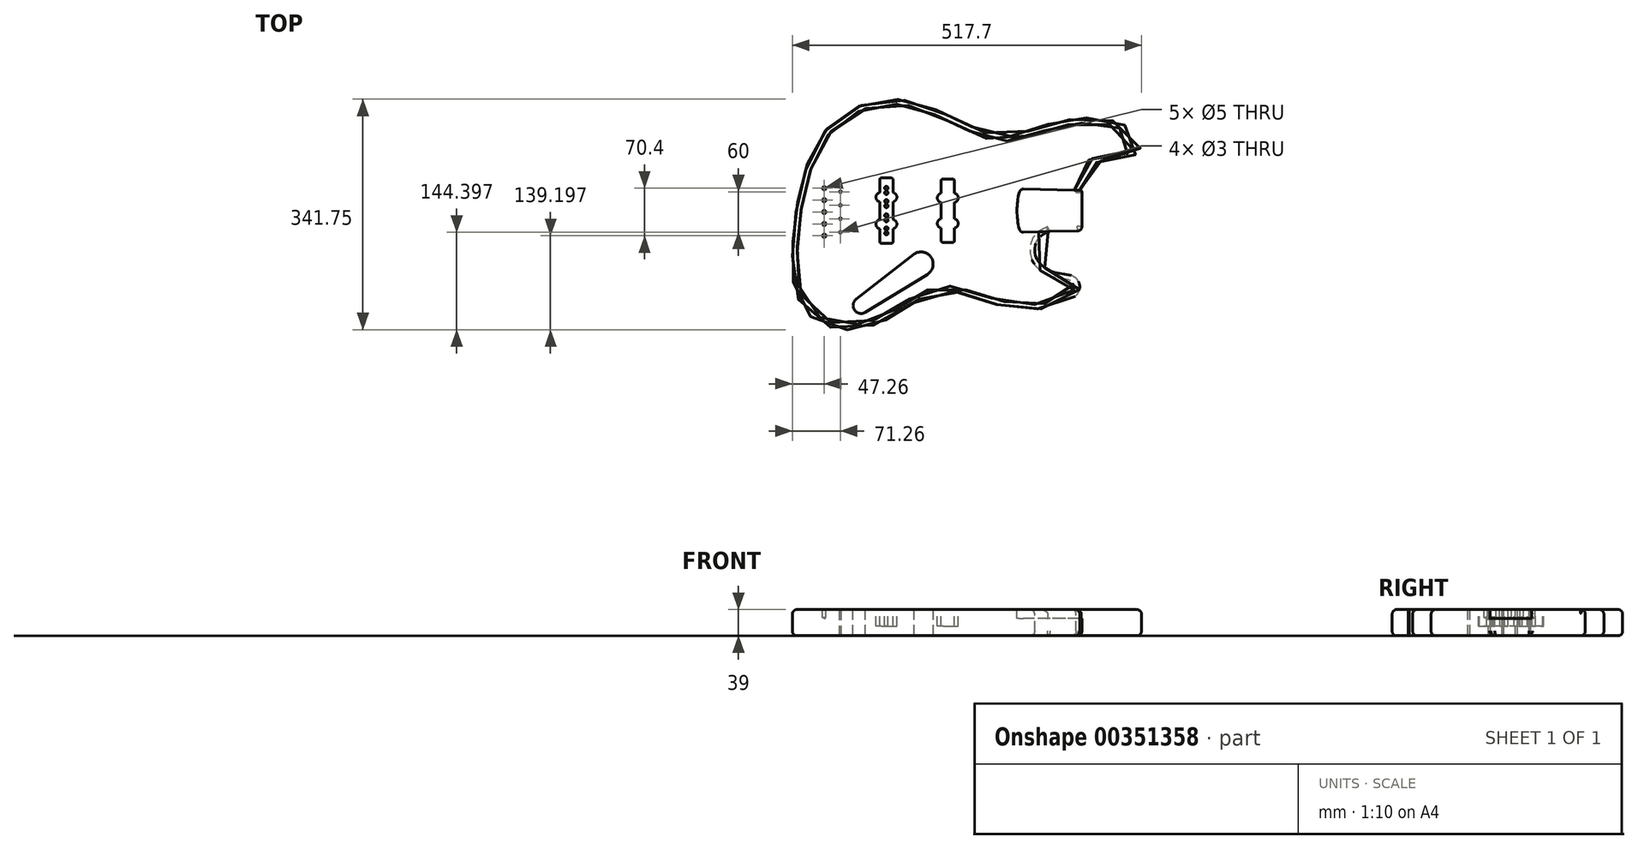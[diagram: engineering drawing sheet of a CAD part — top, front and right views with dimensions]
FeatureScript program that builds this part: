
annotation { "Feature Type Name" : "Feature", "Feature Type Description" : "" }
export const myFeature = defineFeature(function(context is Context, id is Id, definition is map)
    precondition{}
    {
        {
            var Q0;
            Q0=qCreatedBy(makeId("Top.planeOp"),FACE);
            var sketch = newSketch(context, id + "F0", { "sketchPlane" : qUnion([Q0])});
            skSolve(sketch);
        }
        {
            var Q0;
            Q0=qCreatedBy(makeId("Top.planeOp"),FACE);
            var sketch = newSketch(context, id + "F1", { "sketchPlane" : qUnion([Q0])});
            skFitSpline(sketch, "E0", {"points": [v(289.6, -29.05) * mm, v(282.8, -32.55) * mm, v(274.5, -39.46) * mm, v(271.1, -45.26) * mm, v(269.09, -54.77) * mm, v(271.6, -68.78) * mm, v(280.6, -80.18) * mm, v(290.16, -86.66) * mm, v(298.23, -89.68) * mm, v(304.15, -90.57) * mm, v(313.74, -92.33) * mm, v(322.81, -94.1) * mm, v(331, -99.01) * mm, v(334.35, -104.33) * mm, v(335.78, -110.76) * mm, v(333.88, -119.56) * mm, v(327.1, -126.94) * mm, v(314.12, -135.03) * mm, v(295.68, -140.86) * mm, v(270.69, -144.08) * mm, v(240.34, -142.89) * mm, v(209.4, -136.58) * mm, v(186.79, -130.03) * mm, v(168.58, -123.49) * mm, v(156.92, -119.44) * mm, v(143.35, -116.94) * mm, v(129.19, -117.66) * mm, v(110.88, -123.12) * mm, v(92.1, -132.54) * mm, v(78.73, -141.94) * mm, v(63.02, -151.93) * mm, v(42.08, -162.88) * mm, v(24.35, -170.02) * mm, v(7.93, -173.23) * mm, v(-6.83, -174.54) * mm, v(-29.2, -172.4) * mm, v(-58.12, -159.2) * mm, v(-74.3, -142.3) * mm, v(-85.73, -119.2) * mm, v(-89.54, -95.05) * mm, v(-90.25, -74.22) * mm, v(-89.42, -41.97) * mm, v(-86.33, -8.53) * mm, v(-81.57, 19.8) * mm, v(-72.28, 56.92) * mm, v(-59.79, 92.15) * mm, v(-48.36, 111.66) * mm, v(-27.9, 133.92) * mm, v(-3.38, 151.05) * mm, v(21.25, 161.29) * mm, v(43.5, 166.17) * mm, v(72.9, 166.17) * mm, v(111.46, 155.81) * mm, v(140.02, 143.2) * mm, v(171.8, 127.97) * mm, v(186.79, 121.06) * mm, v(202.97, 114.88) * mm, v(219.75, 112.02) * mm, v(234.99, 112.73) * mm, v(257.36, 119.16) * mm, v(282.59, 127.73) * mm, v(302.82, 133.2) * mm, v(323.88, 137.37) * mm, v(345.06, 139.15) * mm, v(365.65, 138.68) * mm, v(387.9, 134.27) * mm, v(404.69, 127.73) * mm, v(415.16, 121.18) * mm, v(423.73, 112.85) * mm, v(427.3, 104.4) * mm, v(425.87, 95) * mm, v(418.5, 85.24) * mm, v(409.8, 80.25) * mm, v(397.66, 78.1) * mm, v(378.74, 76.44) * mm, v(363.27, 74.18) * mm, v(349.47, 69.77) * mm, v(340.78, 65.6) * mm, v(332.33, 56.09) * mm, v(330.55, 47.4) * mm, v(331.5, 40.02) * mm, v(334.23, 35.26) * mm, v(339, 31.7) * mm], "startDerivative": vector(-807.17, -361.43) * mm, "endDerivative": vector(723.85, -461.92) * mm});
            skLineSegment(sketch, "E1", {"start": v(339, 31.7) * mm, "end": v(339, -27.97) * mm});
            skLineSegment(sketch, "E2", {"start": v(289.6, -29.05) * mm, "end": v(339, -27.97) * mm});
            skSolve(sketch);
        }
        {
            var Q0;
            Q0=makeQuery(id+"F1.imprint","IMPRINT",FACE,{"disambiguationData":[TD([[makeQuery(id+"F1.imprint","IMPRINT",EDGE,{"derivedFrom":sQuery(id+"F1.wireOp",EDGE,"E0")}),-1.0]])]});
            extrude(context, id + "F2", {"entities" : qUnion([Q0]), "oppositeDirection" : true, "depth" : 39 * mm});
        }
        {
            var Q0;
            Q0=makeQuery(id+"F2.opExtrude","CAP_EDGE",EDGE,{"disambiguationData":[OSD([sQuery(id+"F1.wireOp",EDGE,"E0")])],"isStart":true});
            var Q1;
            Q1=makeQuery(id+"F2.opExtrude","CAP_EDGE",EDGE,{"disambiguationData":[OSD([sQuery(id+"F1.wireOp",EDGE,"E0")])],"isStart":false});
            var Q2;
            Q2=makeQuery(id+"F2.opExtrude","CAP_EDGE",EDGE,{"disambiguationData":[OSD([sQuery(id+"F1.wireOp",EDGE,"E2")])],"isStart":false});
            var Q3;
            Q3=makeQuery(id+"F2.opExtrude","CAP_EDGE",EDGE,{"disambiguationData":[OSD([sQuery(id+"F1.wireOp",EDGE,"E1")])],"isStart":false});
            fillet(context, id + "F3", {"entities" : qUnion([Q0, Q1, Q2, Q3]), "radius" : 7 * mm, "tangentPropagation" : true, "allowEdgeOverflow" : false});
        }
        {
            var Q0;
            Q0=qCreatedBy(makeId("Top.planeOp"),FACE);
            var sketch = newSketch(context, id + "F4", { "sketchPlane" : qUnion([Q0])});
            skLineSegment(sketch, "E3", {"start": v(346.15, -28.2) * mm, "end": v(247.58, -30.26) * mm});
            skLineSegment(sketch, "E4", {"start": v(247.58, 1.8) * mm, "end": v(247.58, -30.26) * mm, "construction": true});
            skArc(sketch, "E5", {"start": v(242.72, 1.8) * mm, "mid": v(243.94, -14.41) * mm, "end": v(247.58, -30.26) * mm});
            skLineSegment(sketch, "E6", {"start": v(346.15, 1.8) * mm, "end": v(346.15, -28.2) * mm});
            skLineSegment(sketch, "E7", {"start": v(368.55, 1.8) * mm, "end": v(71.57, 1.8) * mm, "construction": true});
            skLineSegment(sketch, "E8.MirrorCS", {"start": v(346.15, 31.8) * mm, "end": v(247.58, 33.85) * mm});
            skArc(sketch, "E9.MirrorCS", {"start": v(242.72, 1.8) * mm, "mid": v(243.94, 18) * mm, "end": v(247.58, 33.85) * mm});
            skLineSegment(sketch, "E10.MirrorCS", {"start": v(346.15, 1.8) * mm, "end": v(346.15, 31.8) * mm});
            skLineSegment(sketch, "E11", {"start": v(71.57, 1.8) * mm, "end": v(-104.88, 1.8) * mm, "construction": true});
            skSolve(sketch);
        }
        {
            var Q0;
            Q0 = qSketchRegion(id + "F4", true);
            extrude(context, id + "F5", {"entities" : qUnion([Q0]), "operationType" : NewBodyOperationType.REMOVE, "oppositeDirection" : true, "depth" : 13 * mm});
        }
        {
            var Q0;
            Q0=makeQuery(id+"F2.opExtrude","SWEPT_EDGE",EDGE,{"disambiguationData":[OSD([sQuery(id+"F1.wireOp",EDGE,"E0"),sQuery(id+"F1.wireOp",EDGE,"E2")])]});
            fillet(context, id + "F6", {"entities" : qUnion([Q0]), "radius" : 10 * mm, "tangentPropagation" : true, "allowEdgeOverflow" : false});
        }
        {
            var Q0;
            Q0=makeQuery(id+"F2.opExtrude","SWEPT_EDGE",EDGE,{"disambiguationData":[OSD([sQuery(id+"F1.wireOp",EDGE,"E1"),sQuery(id+"F1.wireOp",EDGE,"E2")])]});
            var Q1;
            Q1=makeQuery(id+"F2.opExtrude","SWEPT_EDGE",EDGE,{"disambiguationData":[OSD([sQuery(id+"F1.wireOp",EDGE,"E0"),sQuery(id+"F1.wireOp",EDGE,"E1")])]});
            fillet(context, id + "F7", {"entities" : qUnion([Q0, Q1]), "radius" : 6 * mm, "tangentPropagation" : true, "allowEdgeOverflow" : false});
        }
        {
            var Q0;
            Q0=makeQuery(id+"F5.boolean.opBoolean","COPY",EDGE,{"derivedFrom":makeQuery(id+"F5.opExtrude","SWEPT_EDGE",EDGE,{"disambiguationData":[OSD([sQuery(id+"F4.wireOp",EDGE,"E8.MirrorCS"),sQuery(id+"F4.wireOp",EDGE,"E9.MirrorCS")])]})});
            var Q1;
            Q1=makeQuery(id+"F5.boolean.opBoolean","COPY",EDGE,{"derivedFrom":makeQuery(id+"F5.opExtrude","SWEPT_EDGE",EDGE,{"disambiguationData":[OSD([sQuery(id+"F4.wireOp",EDGE,"E3"),sQuery(id+"F4.wireOp",EDGE,"E5")])]})});
            fillet(context, id + "F8", {"entities" : qUnion([Q0, Q1]), "radius" : 6 * mm, "tangentPropagation" : true, "allowEdgeOverflow" : false});
        }
        {
            var Q0;
            Q0=qCreatedBy(makeId("Top.planeOp"),FACE);
            var sketch = newSketch(context, id + "F9", { "sketchPlane" : qUnion([Q0])});
            skLineSegment(sketch, "E12.bottom", {"start": v(40.12, 49.3) * mm, "end": v(58.12, 49.3) * mm, "construction": true});
            skLineSegment(sketch, "E12.left", {"start": v(40.12, 49.3) * mm, "end": v(40.12, 27.8) * mm, "construction": true});
            skLineSegment(sketch, "E12.right", {"start": v(58.12, 49.3) * mm, "end": v(58.12, 27.8) * mm, "construction": true});
            skLineSegment(sketch, "E13", {"start": v(40.12, 21.8) * mm, "end": v(58.12, 21.8) * mm, "construction": true});
            skArc(sketch, "E14", {"start": v(58.12, 15.8) * mm, "mid": v(63.62, 21.8) * mm, "end": v(58.12, 27.8) * mm, "construction": true});
            skLineSegment(sketch, "E15", {"start": v(49.12, 49.3) * mm, "end": v(49.12, 1.8) * mm, "construction": true});
            skLineSegment(sketch, "E16.trimOffspring", {"start": v(58.12, 15.8) * mm, "end": v(58.12, 1.8) * mm, "construction": true});
            skArc(sketch, "E17.MirrorCS", {"start": v(40.12, 15.8) * mm, "mid": v(34.62, 21.8) * mm, "end": v(40.12, 27.8) * mm, "construction": true});
            skLineSegment(sketch, "E18.trimOffspring", {"start": v(40.12, 15.8) * mm, "end": v(40.12, 1.8) * mm, "construction": true});
            skLineSegment(sketch, "E19.MirrorCS", {"start": v(40.12, -12.2) * mm, "end": v(40.12, 1.8) * mm, "construction": true});
            skArc(sketch, "E20.MirrorCS", {"start": v(40.12, -12.2) * mm, "mid": v(34.62, -18.2) * mm, "end": v(40.12, -24.2) * mm, "construction": true});
            skLineSegment(sketch, "E21.MirrorCS", {"start": v(40.12, -45.7) * mm, "end": v(40.12, -24.2) * mm, "construction": true});
            skLineSegment(sketch, "E22.MirrorCS", {"start": v(40.12, -45.7) * mm, "end": v(58.12, -45.7) * mm, "construction": true});
            skLineSegment(sketch, "E23.MirrorCS", {"start": v(58.12, -45.7) * mm, "end": v(58.12, -24.2) * mm, "construction": true});
            skArc(sketch, "E24.MirrorCS", {"start": v(58.12, -12.2) * mm, "mid": v(63.62, -18.2) * mm, "end": v(58.12, -24.2) * mm, "construction": true});
            skLineSegment(sketch, "E25.MirrorCS", {"start": v(58.12, -12.2) * mm, "end": v(58.12, 1.8) * mm, "construction": true});
            skLineSegment(sketch, "E26.0", {"start": v(39.12, 50.3) * mm, "end": v(39.12, 28.65) * mm});
            skArc(sketch, "E26.1", {"start": v(39.12, 14.94) * mm, "mid": v(33.62, 21.8) * mm, "end": v(39.12, 28.65) * mm});
            skLineSegment(sketch, "E26.2", {"start": v(39.12, 14.94) * mm, "end": v(39.12, 1.8) * mm});
            skLineSegment(sketch, "E26.3", {"start": v(59.12, -11.35) * mm, "end": v(59.12, 1.8) * mm});
            skLineSegment(sketch, "E26.4", {"start": v(59.12, 14.94) * mm, "end": v(59.12, 1.8) * mm});
            skArc(sketch, "E26.5", {"start": v(59.12, 14.94) * mm, "mid": v(64.62, 21.8) * mm, "end": v(59.12, 28.65) * mm});
            skLineSegment(sketch, "E26.6", {"start": v(59.12, 50.3) * mm, "end": v(59.12, 28.65) * mm});
            skArc(sketch, "E26.7", {"start": v(59.12, -11.35) * mm, "mid": v(64.62, -18.2) * mm, "end": v(59.12, -25.06) * mm});
            skLineSegment(sketch, "E26.8", {"start": v(59.12, -46.7) * mm, "end": v(59.12, -25.06) * mm});
            skLineSegment(sketch, "E26.9", {"start": v(39.12, -46.7) * mm, "end": v(59.12, -46.7) * mm});
            skLineSegment(sketch, "E26.10", {"start": v(39.12, 50.3) * mm, "end": v(59.12, 50.3) * mm});
            skLineSegment(sketch, "E26.11", {"start": v(39.12, -46.7) * mm, "end": v(39.12, -25.06) * mm});
            skArc(sketch, "E26.12", {"start": v(39.12, -11.35) * mm, "mid": v(33.62, -18.2) * mm, "end": v(39.12, -25.06) * mm});
            skLineSegment(sketch, "E26.13", {"start": v(39.12, -11.35) * mm, "end": v(39.12, 1.8) * mm});
            skLineSegment(sketch, "E27.bottom", {"start": v(131.12, 47.8) * mm, "end": v(149.12, 47.8) * mm, "construction": true});
            skLineSegment(sketch, "E27.top", {"start": v(131.12, -44.2) * mm, "end": v(149.12, -44.2) * mm, "construction": true});
            skLineSegment(sketch, "E27.left", {"start": v(131.12, 47.8) * mm, "end": v(131.12, 26.8) * mm, "construction": true});
            skLineSegment(sketch, "E27.right", {"start": v(149.12, 47.8) * mm, "end": v(149.12, 26.8) * mm, "construction": true});
            skPoint(sketch, "E28", {"position": v(149.12, 1.8) * mm});
            skArc(sketch, "E29", {"start": v(149.12, 14.8) * mm, "mid": v(154.62, 20.8) * mm, "end": v(149.12, 26.8) * mm, "construction": true});
            skLineSegment(sketch, "E30", {"start": v(140.12, 47.8) * mm, "end": v(140.12, -44.2) * mm, "construction": true});
            skArc(sketch, "E31.MirrorCS", {"start": v(131.12, 14.8) * mm, "mid": v(125.62, 20.8) * mm, "end": v(131.12, 26.8) * mm, "construction": true});
            skArc(sketch, "E32.MirrorCS", {"start": v(131.12, -11.2) * mm, "mid": v(125.62, -17.2) * mm, "end": v(131.12, -23.2) * mm, "construction": true});
            skArc(sketch, "E33.MirrorCS", {"start": v(149.12, -11.2) * mm, "mid": v(154.62, -17.2) * mm, "end": v(149.12, -23.2) * mm, "construction": true});
            skLineSegment(sketch, "E34.trimOffspring", {"start": v(131.12, 14.8) * mm, "end": v(131.12, -11.2) * mm, "construction": true});
            skLineSegment(sketch, "E35.trimOffspring", {"start": v(149.12, 14.8) * mm, "end": v(149.12, -11.2) * mm, "construction": true});
            skLineSegment(sketch, "E36.trimOffspring", {"start": v(149.12, -23.2) * mm, "end": v(149.12, -44.2) * mm, "construction": true});
            skLineSegment(sketch, "E37.trimOffspring", {"start": v(131.12, -23.2) * mm, "end": v(131.12, -44.2) * mm, "construction": true});
            skLineSegment(sketch, "E38.0", {"start": v(130.12, 48.8) * mm, "end": v(130.12, 27.65) * mm});
            skArc(sketch, "E38.1", {"start": v(150.12, -10.35) * mm, "mid": v(155.62, -17.2) * mm, "end": v(150.12, -24.06) * mm});
            skLineSegment(sketch, "E38.2", {"start": v(150.12, 13.94) * mm, "end": v(150.12, -10.35) * mm});
            skArc(sketch, "E38.3", {"start": v(150.12, 13.94) * mm, "mid": v(155.62, 20.8) * mm, "end": v(150.12, 27.65) * mm});
            skLineSegment(sketch, "E38.4", {"start": v(150.12, 48.8) * mm, "end": v(150.12, 27.65) * mm});
            skLineSegment(sketch, "E38.5", {"start": v(150.12, -24.06) * mm, "end": v(150.12, -45.2) * mm});
            skLineSegment(sketch, "E38.6", {"start": v(130.12, 48.8) * mm, "end": v(150.12, 48.8) * mm});
            skLineSegment(sketch, "E38.7", {"start": v(130.12, -45.2) * mm, "end": v(150.12, -45.2) * mm});
            skLineSegment(sketch, "E38.8", {"start": v(130.12, -24.06) * mm, "end": v(130.12, -45.2) * mm});
            skArc(sketch, "E38.9", {"start": v(130.12, -10.35) * mm, "mid": v(124.62, -17.2) * mm, "end": v(130.12, -24.06) * mm});
            skLineSegment(sketch, "E38.10", {"start": v(130.12, 13.94) * mm, "end": v(130.12, -10.35) * mm});
            skArc(sketch, "E38.11", {"start": v(130.12, 13.94) * mm, "mid": v(124.62, 20.8) * mm, "end": v(130.12, 27.65) * mm});
            skCircle(sketch, "E39", {"center": v(49.12, 35.3) * mm, "radius": 2.5 * mm});
            skCircle(sketch, "E40", {"center": v(49.12, 28.3) * mm, "radius": 2.5 * mm});
            skLineSegment(sketch, "E41", {"start": v(49.12, 35.3) * mm, "end": v(49.12, 28.3) * mm, "construction": true});
            skPoint(sketch, "E42", {"position": v(49.12, 31.8) * mm});
            skCircle(sketch, "E43.0.1.0", {"center": v(49.12, 15.8) * mm, "radius": 2.5 * mm});
            skCircle(sketch, "E43.0.1.1", {"center": v(49.12, 8.8) * mm, "radius": 2.5 * mm});
            skLineSegment(sketch, "E43.direction1", {"start": v(49.12, 35.3) * mm, "end": v(74.12, 35.3) * mm, "construction": true});
            skLineSegment(sketch, "E43.direction2", {"start": v(49.12, 35.3) * mm, "end": v(49.12, 15.8) * mm, "construction": true});
            skCircle(sketch, "E44.MirrorC", {"center": v(49.12, -31.7) * mm, "radius": 2.5 * mm});
            skCircle(sketch, "E45.MirrorC", {"center": v(49.12, -24.7) * mm, "radius": 2.5 * mm});
            skCircle(sketch, "E46.MirrorC", {"center": v(49.12, -12.2) * mm, "radius": 2.5 * mm});
            skCircle(sketch, "E47.MirrorC", {"center": v(49.12, -5.2) * mm, "radius": 2.5 * mm});
            skSolve(sketch);
        }
        {
            var Q0;
            Q0 = qSketchRegion(id + "F9", true);
            extrude(context, id + "F10", {"entities" : qUnion([Q0]), "operationType" : NewBodyOperationType.REMOVE, "oppositeDirection" : true, "depth" : 25 * mm});
        }
        {
            var Q0;
            Q0=qCreatedBy(makeId("Top.planeOp"),FACE);
            var sketch = newSketch(context, id + "F11", { "sketchPlane" : qUnion([Q0])});
            skPoint(sketch, "E48", {"position": v(-43, 35) * mm});
            skPoint(sketch, "E49.0.1.0", {"position": v(-43, 17.4) * mm});
            skPoint(sketch, "E49.0.2.0", {"position": v(-43, -0.2) * mm});
            skPoint(sketch, "E49.0.3.0", {"position": v(-43, -17.8) * mm});
            skPoint(sketch, "E49.0.4.0", {"position": v(-43, -35.4) * mm});
            skLineSegment(sketch, "E49.direction1", {"start": v(-43, 35) * mm, "end": v(-17.85, 35) * mm, "construction": true});
            skLineSegment(sketch, "E49.direction2", {"start": v(-43, 35) * mm, "end": v(-43, 17.4) * mm, "construction": true});
            skSolve(sketch);
        }
        {
            var Q0;
            Q0=sQuery(id+"F11.wireOp",VERTEX,"E48");
            var Q1;
            Q1=sQuery(id+"F11.wireOp",VERTEX,"E49.0.1.0");
            var Q2;
            Q2=sQuery(id+"F11.wireOp",VERTEX,"E49.0.2.0");
            var Q3;
            Q3=sQuery(id+"F11.wireOp",VERTEX,"E49.0.3.0");
            var Q4;
            Q4=sQuery(id+"F11.wireOp",VERTEX,"E49.0.4.0");
            var Q5;
            Q5=makeQuery(id+"F2.opExtrude","SWEPT_BODY",BODY,{"disambiguationData":[OSD([sQuery(id+"F1.wireOp",EDGE,"E0"),sQuery(id+"F1.wireOp",EDGE,"E1"),sQuery(id+"F1.wireOp",EDGE,"E2")])]});
            hole(context, id + "F12", {"style" : HoleStyle.SIMPLE, "endStyle" : HoleEndStyle.BLIND, "holeDiameter" : 5 * mm, "holeDepth" : 12 * mm, "isTappedThrough" : true, "tappedDepth" : 12 * mm, "tapClearance" : 3, "locations" : qUnion([Q0, Q1, Q2, Q3, Q4]), "scope" : qUnion([Q5])});
        }
        {
            var Q0;
            Q0=qCreatedBy(makeId("Top.planeOp"),FACE);
            var sketch = newSketch(context, id + "F13", { "sketchPlane" : qUnion([Q0])});
            skCircle(sketch, "E50", {"center": v(12.31, -137.75) * mm, "radius": 7.25 * mm, "construction": true});
            skCircle(sketch, "E51", {"center": v(40.47, -118.34) * mm, "radius": 10.1 * mm, "construction": true});
            skCircle(sketch, "E52", {"center": v(70.14, -97.6) * mm, "radius": 12.64 * mm, "construction": true});
            skCircle(sketch, "E53", {"center": v(99.44, -77.82) * mm, "radius": 12.36 * mm, "construction": true});
            skLineSegment(sketch, "E54", {"start": v(4.32, -129.38) * mm, "end": v(90.5, -62.42) * mm});
            skLineSegment(sketch, "E55", {"start": v(17.64, -149.16) * mm, "end": v(109.88, -92.67) * mm});
            skArc(sketch, "E56", {"start": v(109.88, -92.67) * mm, "mid": v(115.63, -67.66) * mm, "end": v(90.5, -62.42) * mm});
            skArc(sketch, "E57", {"start": v(4.32, -129.38) * mm, "mid": v(1.74, -145.49) * mm, "end": v(17.64, -149.16) * mm});
            skSolve(sketch);
        }
        {
            var Q0;
            Q0=makeQuery(id+"F13.imprint","IMPRINT",FACE,{"disambiguationData":[TD([[makeQuery(id+"F13.imprint","IMPRINT",EDGE,{"derivedFrom":sQuery(id+"F13.wireOp",EDGE,"E54")}),-1.0]])]});
            extrude(context, id + "F14", {"entities" : qUnion([Q0]), "operationType" : NewBodyOperationType.REMOVE, "oppositeDirection" : true, "depth" : 38 * mm});
        }
        {
            var Q0;
            Q0=qCreatedBy(makeId("Top.planeOp"),FACE);
            var sketch = newSketch(context, id + "F15", { "sketchPlane" : qUnion([Q0])});
            skPoint(sketch, "E58", {"position": v(-19, -0.2) * mm});
            skCircle(sketch, "E59", {"center": v(-19, 9.8) * mm, "radius": 1.5 * mm});
            skCircle(sketch, "E60", {"center": v(-19, 29.8) * mm, "radius": 1.5 * mm});
            skCircle(sketch, "E61.MirrorC", {"center": v(-19, -10.2) * mm, "radius": 1.5 * mm});
            skCircle(sketch, "E62.MirrorC", {"center": v(-19, -30.2) * mm, "radius": 1.5 * mm});
            skLineSegment(sketch, "E63", {"start": v(-19, 29.8) * mm, "end": v(-19, 9.8) * mm, "construction": true});
            skLineSegment(sketch, "E64", {"start": v(-19, 9.8) * mm, "end": v(-19, -10.2) * mm, "construction": true});
            skLineSegment(sketch, "E65", {"start": v(-19, -10.2) * mm, "end": v(-19, -30.2) * mm, "construction": true});
            skSolve(sketch);
        }
        {
            var Q0;
            Q0 = qSketchRegion(id + "F15", true);
            extrude(context, id + "F16", {"entities" : qUnion([Q0]), "operationType" : NewBodyOperationType.REMOVE, "endBound" : BoundingType.THROUGH_ALL, "oppositeDirection" : true, "depth" : 25 * mm});
        }
        {
            var Q0;
            Q0=qCreatedBy(makeId("Top.planeOp"),FACE);
            var sketch = newSketch(context, id + "F17", { "sketchPlane" : qUnion([Q0])});
            skLineSegment(sketch, "E66", {"start": v(247.58, 33.85) * mm, "end": v(850.36, 21.3) * mm});
            skLineSegment(sketch, "E67.MirrorCS", {"start": v(247.58, -30.26) * mm, "end": v(850.36, -17.7) * mm});
            skSolve(sketch);
        }
        {
            var Q0;
            Q0=makeQuery(id+"F10.boolean.opBoolean","COPY",EDGE,{"derivedFrom":makeQuery(id+"F10.opExtrude","SWEPT_EDGE",EDGE,{"disambiguationData":[OSD([sQuery(id+"F9.wireOp",EDGE,"E26.0"),sQuery(id+"F9.wireOp",EDGE,"E26.10")])]})});
            var Q1;
            Q1=makeQuery(id+"F10.boolean.opBoolean","COPY",EDGE,{"derivedFrom":makeQuery(id+"F10.opExtrude","SWEPT_EDGE",EDGE,{"disambiguationData":[OSD([sQuery(id+"F9.wireOp",EDGE,"E38.0"),sQuery(id+"F9.wireOp",EDGE,"E38.6")])]})});
            var Q2;
            Q2=makeQuery(id+"F10.boolean.opBoolean","COPY",EDGE,{"derivedFrom":makeQuery(id+"F10.opExtrude","SWEPT_EDGE",EDGE,{"disambiguationData":[OSD([sQuery(id+"F9.wireOp",EDGE,"E26.6"),sQuery(id+"F9.wireOp",EDGE,"E26.10")])]})});
            var Q3;
            Q3=makeQuery(id+"F10.boolean.opBoolean","COPY",EDGE,{"derivedFrom":makeQuery(id+"F10.opExtrude","SWEPT_EDGE",EDGE,{"disambiguationData":[OSD([sQuery(id+"F9.wireOp",EDGE,"E38.4"),sQuery(id+"F9.wireOp",EDGE,"E38.6")])]})});
            var Q4;
            Q4=makeQuery(id+"F10.boolean.opBoolean","COPY",EDGE,{"derivedFrom":makeQuery(id+"F10.opExtrude","SWEPT_EDGE",EDGE,{"disambiguationData":[OSD([sQuery(id+"F9.wireOp",EDGE,"E26.9"),sQuery(id+"F9.wireOp",EDGE,"E26.11")])]})});
            var Q5;
            Q5=makeQuery(id+"F10.boolean.opBoolean","COPY",EDGE,{"derivedFrom":makeQuery(id+"F10.opExtrude","SWEPT_EDGE",EDGE,{"disambiguationData":[OSD([sQuery(id+"F9.wireOp",EDGE,"E38.7"),sQuery(id+"F9.wireOp",EDGE,"E38.8")])]})});
            var Q6;
            Q6=makeQuery(id+"F10.boolean.opBoolean","COPY",EDGE,{"derivedFrom":makeQuery(id+"F10.opExtrude","SWEPT_EDGE",EDGE,{"disambiguationData":[OSD([sQuery(id+"F9.wireOp",EDGE,"E38.5"),sQuery(id+"F9.wireOp",EDGE,"E38.7")])]})});
            var Q7;
            Q7=makeQuery(id+"F10.boolean.opBoolean","COPY",EDGE,{"derivedFrom":makeQuery(id+"F10.opExtrude","SWEPT_EDGE",EDGE,{"disambiguationData":[OSD([sQuery(id+"F9.wireOp",EDGE,"E26.8"),sQuery(id+"F9.wireOp",EDGE,"E26.9")])]})});
            fillet(context, id + "F18", {"entities" : qUnion([Q0, Q1, Q2, Q3, Q4, Q5, Q6, Q7]), "radius" : 3 * mm, "tangentPropagation" : true, "allowEdgeOverflow" : false});
        }
    });
